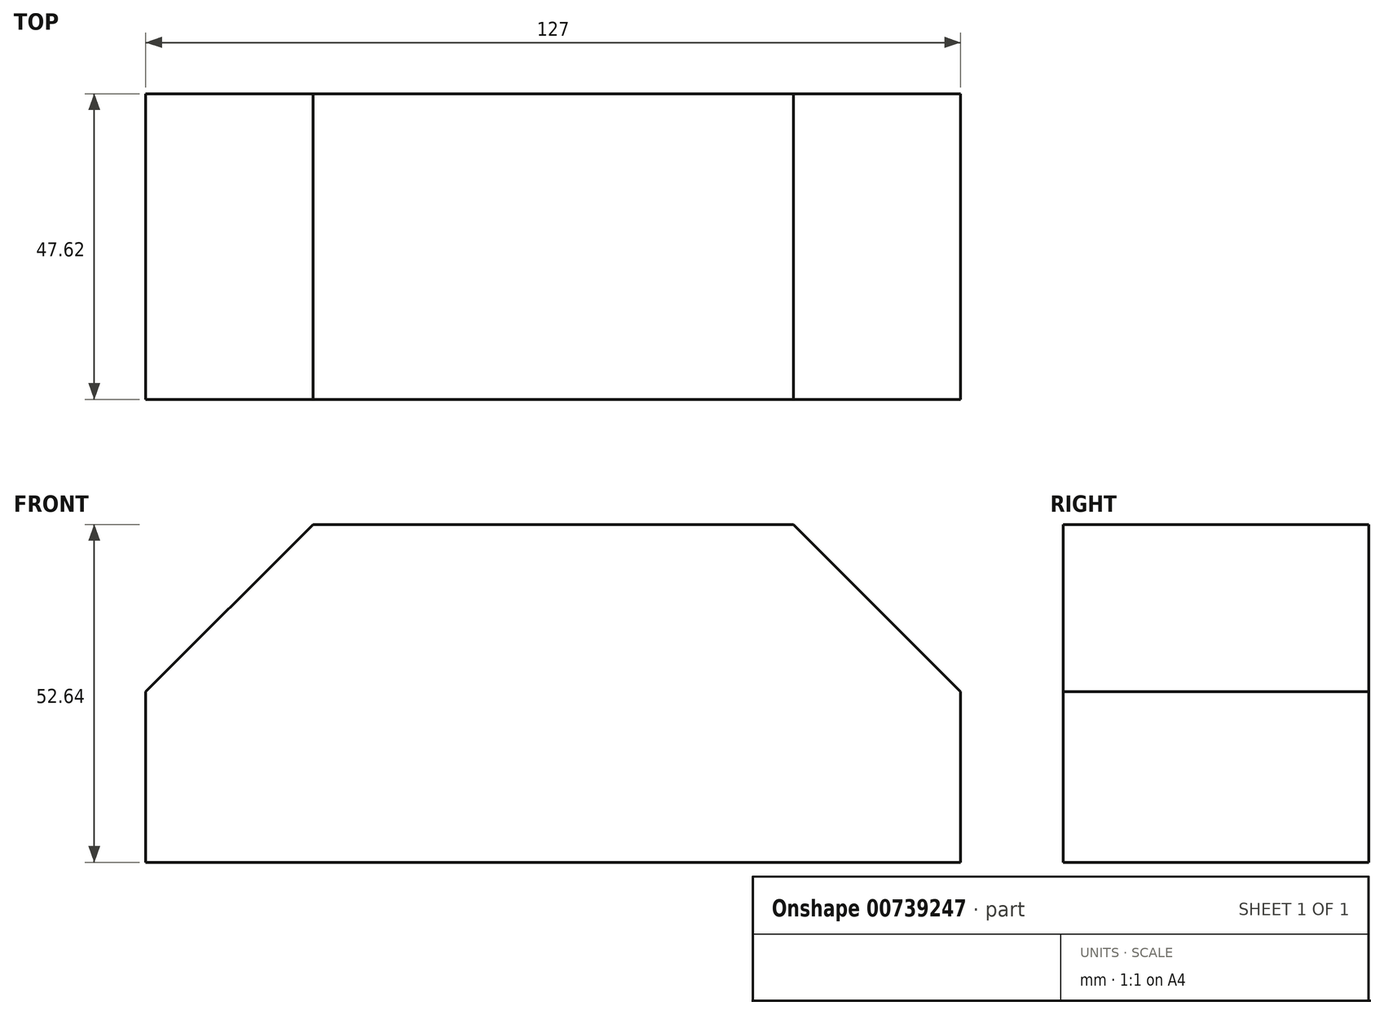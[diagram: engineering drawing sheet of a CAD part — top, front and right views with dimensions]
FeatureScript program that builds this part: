
annotation { "Feature Type Name" : "Feature", "Feature Type Description" : "" }
export const myFeature = defineFeature(function(context is Context, id is Id, definition is map)
    precondition{}
    {
        {
            var Q0;
            Q0=qCreatedBy(makeId("Front.planeOp"),FACE);
            var sketch = newSketch(context, id + "F0", { "sketchPlane" : qUnion([Q0])});
            skLineSegment(sketch, "E0", {"start": v(-70.87, -26.58) * mm, "end": v(56.13, -26.58) * mm});
            skLineSegment(sketch, "E1", {"start": v(56.13, -26.58) * mm, "end": v(56.13, 0) * mm});
            skLineSegment(sketch, "E2", {"start": v(56.13, 0) * mm, "end": v(30.07, 26.06) * mm});
            skLineSegment(sketch, "E3", {"start": v(30.07, 26.06) * mm, "end": v(-44.81, 26.06) * mm});
            skLineSegment(sketch, "E4", {"start": v(-44.81, 26.06) * mm, "end": v(-70.87, 0) * mm});
            skLineSegment(sketch, "E5", {"start": v(-70.87, 0) * mm, "end": v(-70.87, -26.58) * mm});
            skSolve(sketch);
        }
        {
            var Q0;
            Q0=makeQuery(id+"F0.imprint","IMPRINT",FACE,{"disambiguationData":[TD([[makeQuery(id+"F0.imprint","IMPRINT",EDGE,{"derivedFrom":sQuery(id+"F0.wireOp",EDGE,"E0")}),1.0]])]});
            extrude(context, id + "F1", {"entities" : qUnion([Q0]), "depth" : 47.62 * mm, "offsetDistance" : 25.4 * mm});
        }
    });
